# Revit family: QF_BOURGEAT_Satellite4G_2GN16_chaud_2-1
name_source: partatom
category: Equipement spécialisé
revit_build: Autodesk Revit 2015 (Build: 20140606_1530(x64)
units: mm (PartAtom-declared; Revit-internal decimal feet)

## types (2) — shared parameters
Certification = NF hygiene alimentaire
Charge max = 300.00 kg
Consommation énergétique = 1.28Kwh/h NFD40-016
Diametre_roue = 160 mm  [stored 0.524934 ft]
Fabricant = BOURGEAT
Fréquence = 50 Hz
Hauteur hors tout = 1848 mm  [stored 6.06299 ft]
Hauteur_poignee_porte_sol_porte_basse = 283 mm  [stored 0.928478 ft]
Hauteur_poignee_porte_sol_porte_haute = 283 mm  [stored 0.928478 ft]
Hauteur_poignees_laterales = 905 mm  [stored 2.96916 ft]
Hauteur_porte = 1601 mm  [stored 5.25262 ft]
Hauteur_porte_basse = 758 mm  [stored 2.48688 ft]
Hauteur_porte_haute = 758 mm  [stored 2.48688 ft]
Hauteur_roue = 200 mm  [stored 0.656168 ft]
Indice de protection = IP25
Largeur_porte = 706 mm  [stored 2.31627 ft]
Longueur hors tout = 791 mm
Longueur_poignees_laterales = 803 mm  [stored 2.63451 ft]
Materiau_Poignee_porte = B_Elastomère_TPE_S
Materiau_bac = B_Elastomère_TPE_S
Materiau_bandage = B_Elastomère_TPE_S
Materiau_porte = Acier inoxydable, brossé
Materiau_vitre = Verre, vitrage transparent, trempé
Nature isolant = Mousse sans PU
Phase = 2
Poignee_droite = Oui
Poignee_gauche = Non
Pos_V_IHM = 197 mm
Profondeur hors tout = 959 mm  [stored 3.14633 ft]
Spécification du Fabricant = Satellite 4G
Tension = 230 V
URL catalogue = http://www.bourgeat.fr

## per-type parameters (varying)
| type | Humidification | Intensité nominale | Modèle | Poids net à vide | Puissance électrique  |
| 2GN16_sans_humidification | Non | 8 A | 840232 | 140.00 kg | 1900 W |
| 2GN16_humidification | Oui | 15 A | 840332 | 114.00 kg | 3500 W |

note: [stored X ft] marks values corroborated as IEEE doubles in the binary element streams (Revit-internal decimal feet)
